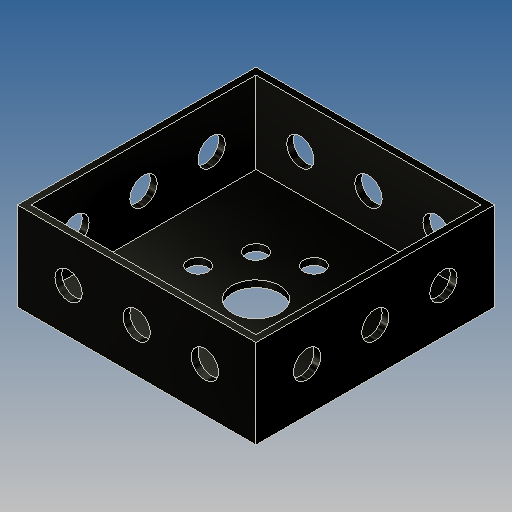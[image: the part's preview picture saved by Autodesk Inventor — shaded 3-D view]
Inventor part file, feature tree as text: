
AUTODESK INVENTOR PART (.ipt)
format: ipt  version: 2020 (Build 240168000, 168)  size: 208,896 bytes
history: native  units: mm
features: extrude x4, sketch x4, other x1, projected_geometry x1
ambient origin geometry x8: Origin, YZ Plane, XZ Plane, XY Plane, X Axis, Y Axis, Z Axis, Center Point
bodies: Body1 (feature_tree)
feature tree (10):
  other  "Твердое тело1"
  extrude  "Выдавливание1"  Depth=7.0mm
  extrude  "Выдавливание2"  Depth=3.0mm
  extrude  "Выдавливание3"  Depth=8.5mm
  extrude  "Выдавливание4"  Depth=80.0mm TaperAngle=360.0deg
  sketch  "Эскиз1"
  sketch  "Эскиз2"
  projected_geometry  "Спроецированная петля1"
  sketch  "Эскиз3"
  sketch  "Эскиз4"
